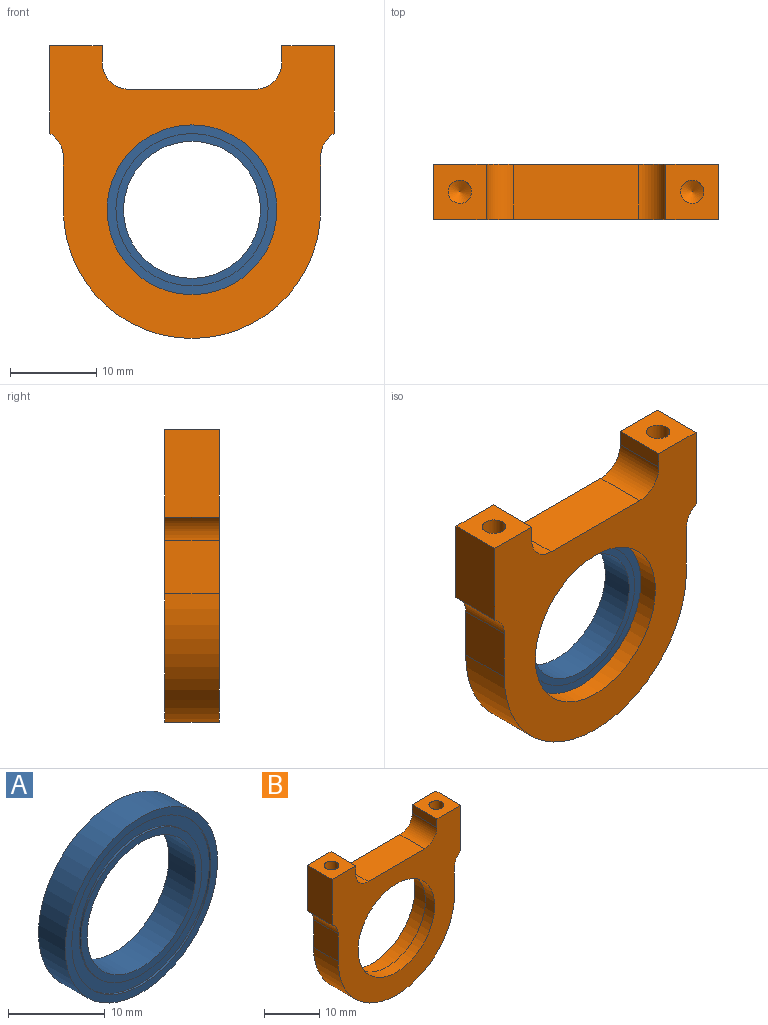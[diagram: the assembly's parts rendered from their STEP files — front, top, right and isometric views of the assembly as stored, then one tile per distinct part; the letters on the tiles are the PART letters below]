
ASSEMBLY  parts=2 mates=1
PART A: 12 faces, bbox 22.2x3.9x22.2 mm
  f0: cylinder r=8.83mm len=17.65mm, axis (0,-1,0), area 14.1mm2, adj f6,f11
  f1: cylinder r=10.16mm len=20.32mm, axis (0,-1,0), area 16.2mm2, adj f9,f11
  f2: cylinder r=8.83mm len=17.65mm, axis (0,1,0), area 14.1mm2, adj f7,f10
  f3: cylinder r=10.16mm len=20.32mm, axis (0,1,0), area 16.2mm2, adj f8,f10
  f4: cylinder r=7.94mm len=15.88mm, axis (0,-1,0), area 195.1mm2, adj f6,f7
  f5: cylinder r=11.11mm len=22.23mm, axis (0,-1,0), area 273.1mm2, adj f8,f9
  f6: plane 17.65x17.65mm, normal (0,-1,0), area 46.8mm2, adj f0,f4
  f7: plane 17.65x17.65mm, normal (0,1,0), area 46.8mm2, adj f2,f4
  f8: plane 22.23x22.23mm, normal (0,1,0), area 63.7mm2, adj f3,f5
  f9: plane 22.23x22.23mm, normal (0,-1,0), area 63.7mm2, adj f1,f5
  f10: plane 20.32x20.32mm, normal (0,1,0), area 79.5mm2, adj f2,f3
  f11: plane 20.32x20.32mm, normal (0,-1,0), area 79.5mm2, adj f0,f1
PART B: 23 faces, bbox 33x6.4x34 mm
  f0: cylinder r=9.84mm len=19.69mm, axis (0,1,0), area 147.7mm2, adj f17,f22
  f1: cylinder r=11.11mm len=22.23mm, axis (0,1,0), area 276.7mm2, adj f16,f22
  f2: cylinder r=1.35mm len=7.62mm, axis (0,0,1), area 64.8mm2, adj f3,f9
  f3: cone r=1.35mm half-angle=59deg, axis (0,0,1), area 6.7mm2, adj f2
  f4: cylinder r=1.35mm len=7.62mm, axis (0,0,1), area 64.8mm2, adj f5,f13
  f5: cone r=1.35mm half-angle=59deg, axis (0,0,1), area 6.7mm2, adj f4
  f6: cylinder r=14.92mm len=29.85mm, axis (0,-1,0), area 297.7mm2, adj f7,f15,f16,f17
  f7: plane 6.35x6.14mm, normal (-1,0,0), area 39mm2, adj f6,f16,f17,f18
  f8: plane 10.16x6.35mm, normal (-1,0,0), area 64.5mm2, adj f9,f16,f17,f18
  f9: plane 6.35x6.08mm, normal (0,0,1), area 32.9mm2, adj f2,f8,f10,f16,f17
  f10: plane 6.35x1.91mm, normal (1,0,0), area 12.1mm2, adj f9,f16,f17,f21
  f11: plane 14.51x6.35mm, normal (0,0,1), area 92.1mm2, adj f16,f17,f20,f21
  f12: plane 6.35x1.91mm, normal (-1,0,0), area 12.1mm2, adj f13,f16,f17,f20
  f13: plane 6.35x6.08mm, normal (0,0,1), area 32.9mm2, adj f4,f12,f14,f16,f17
  f14: plane 10.16x6.35mm, normal (1,0,0), area 64.5mm2, adj f13,f16,f17,f19
  f15: plane 6.35x6.14mm, normal (1,0,0), area 39mm2, adj f6,f16,f17,f19
  f16: plane 33.97x33.02mm, normal (0,1,0), area 463.5mm2, adj f1,f6,f7,f8,f9,f10,f11,f12
  f17: plane 33.97x33.02mm, normal (0,-1,0), area 547.2mm2, adj f0,f6,f7,f8,f9,f10,f11,f12
  f18: cylinder r=3.17mm len=6.35mm, axis (0,1,0), area 21.1mm2, adj f7,f8,f16,f17
  f19: cylinder r=3.17mm len=6.35mm, axis (0,-1,0), area 21.1mm2, adj f14,f15,f16,f17
  f20: cylinder r=3.17mm len=6.35mm, axis (0,1,0), area 31.7mm2, adj f11,f12,f16,f17
  f21: cylinder r=3.17mm len=6.35mm, axis (0,1,0), area 31.7mm2, adj f10,f11,f16,f17
  f22: plane 22.23x22.23mm, normal (0,1,0), area 83.6mm2, adj f0,f1
PLACE A rot(axis=(0,1,0),0deg) t=(14.5,17.36,22.77)mm
PLACE B t=(14.5,14.97,22.77)mm
MATE fastened A.f0 <-> B.f0  axis (0,1,0) through (14.5,17.36,22.77)mm
